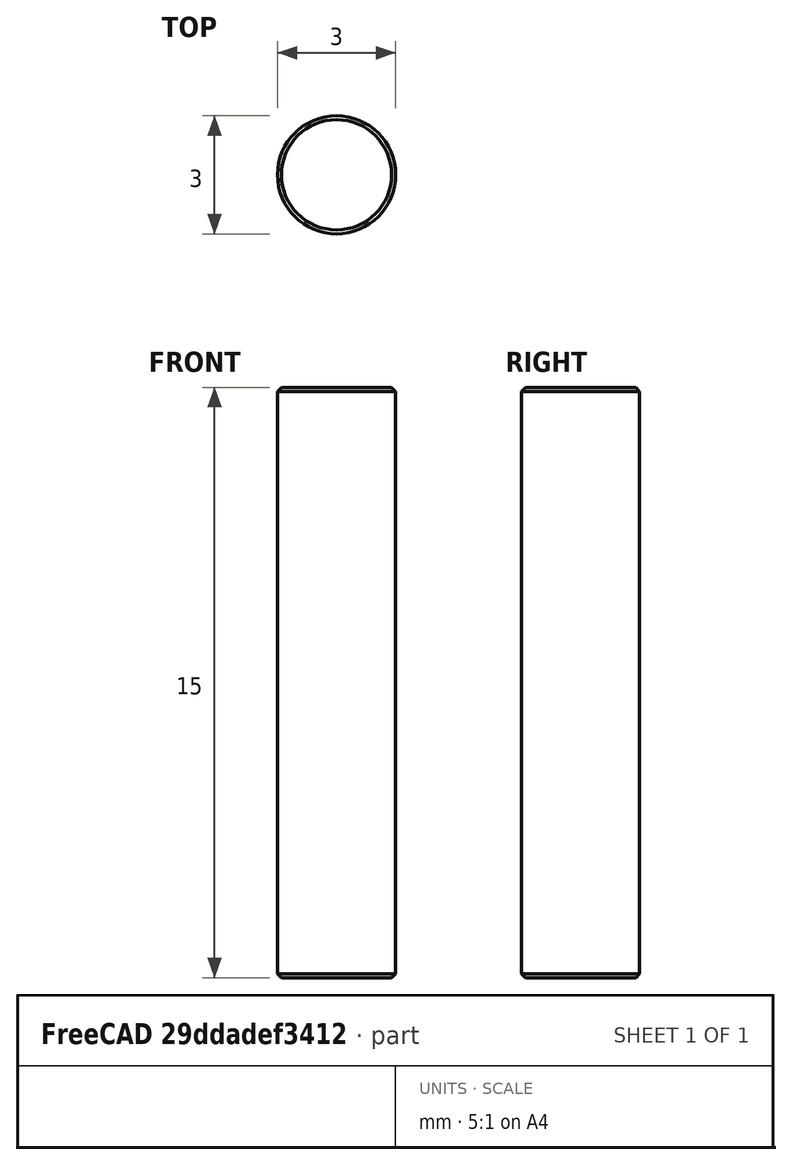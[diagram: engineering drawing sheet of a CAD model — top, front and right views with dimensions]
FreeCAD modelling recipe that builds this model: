
FCSTD DOCUMENT  (FreeCAD 0.18R15969 (Git))
Label: magnet_15x3mm
License: All rights reserved
LicenseURL: http://en.wikipedia.org/wiki/All_rights_reserved
objects: Sketcher::SketchObject×1, PartDesign::Pad×1, PartDesign::Chamfer×1, PartDesign::Body×1
note: 5 computed .brp shape members not serialized (recipe doc carries the construction recipe); baked Part::Feature solids carry a one-line shape summary decoded from their .brp

FEATURE [Sketcher::SketchObject] Sketch
  MapMode = 5
  Support = -> [XY_Plane]
  sketch-geometry (1):
    g0: Circle CenterX=0 CenterY=0 CenterZ=0 NormalX=0 NormalY=0 NormalZ=1 AngleXU=0 Radius=1.5
  constraints (2):
    c: Coincident(g0,g-1)
    c: Radius(g0) = 1.5
FEATURE [PartDesign::Pad] Pad
  Length = 15
  Length2 = 100
  Profile = -> Sketch
  Refine = true
  Reversed = true
  Type = 0
FEATURE [PartDesign::Chamfer] Chamfer
  Base = -> Pad [Edge2,Edge3]
  BaseFeature = -> Pad
  Size = 0.1
FEATURE [PartDesign::Body] Body
  Group = -> [Sketch,Pad,Chamfer]
  Origin = -> Origin
  Tip = -> Chamfer
